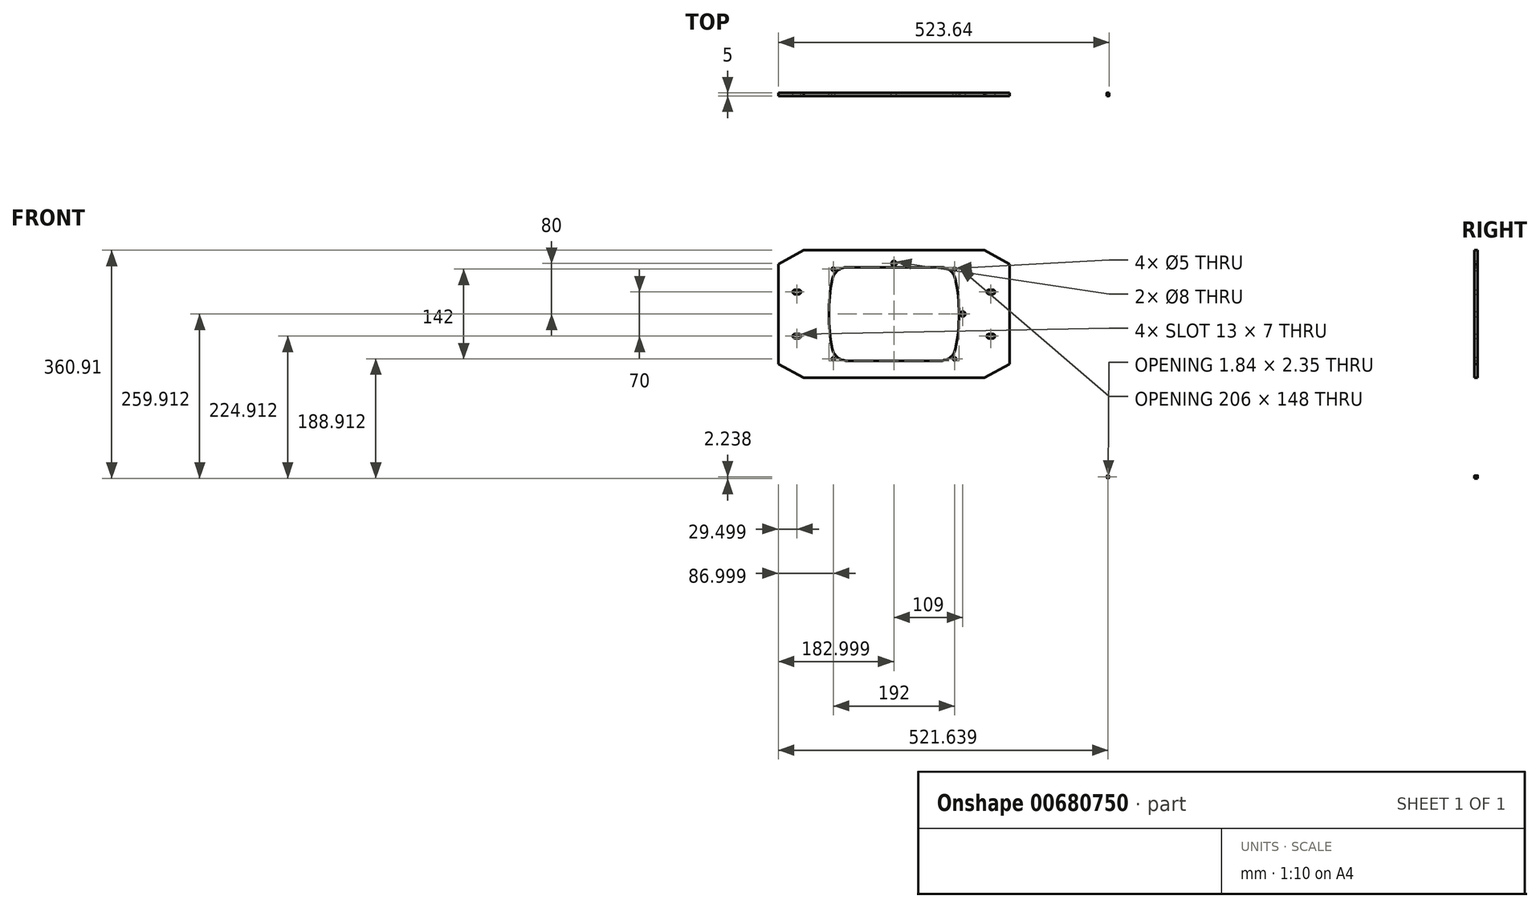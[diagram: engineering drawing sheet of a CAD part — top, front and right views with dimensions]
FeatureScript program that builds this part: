
annotation { "Feature Type Name" : "Feature", "Feature Type Description" : "" }
export const myFeature = defineFeature(function(context is Context, id is Id, definition is map)
    precondition{}
    {
        {
            var Q0;
            Q0=qCreatedBy(makeId("Front.planeOp"),FACE);
            var sketch = newSketch(context, id + "F0", { "sketchPlane" : qUnion([Q0])});
            skFitSpline(sketch, "E0", {"points": [v(706.62, 27.8) * mm, v(706.65, 27.8) * mm, v(706.71, 27.8) * mm, v(706.82, 27.8) * mm, v(707.08, 27.76) * mm, v(707.3, 27.69) * mm, v(707.52, 27.62) * mm, v(707.88, 27.38) * mm, v(708.07, 27.17) * mm, v(708.23, 27) * mm, v(708.36, 26.76) * mm, v(708.5, 26.42) * mm, v(708.6, 26.12) * mm, v(708.63, 25.77) * mm, v(708.65, 25.46) * mm, v(708.6, 25.09) * mm, v(708.56, 24.86) * mm, v(708.36, 24.37) * mm, v(708.23, 24.2) * mm, v(708.05, 23.94) * mm, v(707.84, 23.77) * mm, v(707.61, 23.62) * mm, v(707.37, 23.5) * mm, v(707.09, 23.41) * mm, v(706.82, 23.38) * mm, v(706.47, 23.34) * mm, v(706, 23.49) * mm, v(705.8, 23.57) * mm, v(705.54, 23.73) * mm, v(705.32, 23.92) * mm, v(705.15, 24.07) * mm, v(704.9, 24.49) * mm, v(704.82, 24.73) * mm, v(704.71, 25.11) * mm, v(704.65, 25.38) * mm, v(704.7, 25.99) * mm, v(704.76, 26.27) * mm, v(704.86, 26.62) * mm, v(705, 26.9) * mm, v(705.18, 27.14) * mm, v(705.43, 27.37) * mm, v(705.58, 27.5) * mm, v(706.03, 27.72) * mm, v(706.16, 27.74) * mm, v(706.42, 27.8) * mm, v(706.53, 27.8) * mm, v(706.59, 27.8) * mm, v(706.62, 27.8) * mm]});
            skFitSpline(sketch, "E1", {"points": [v(706.63, 26.75) * mm, v(706.65, 26.75) * mm, v(706.7, 26.75) * mm, v(706.76, 26.75) * mm, v(706.88, 26.73) * mm, v(706.94, 26.7) * mm, v(707.03, 26.67) * mm, v(707.1, 26.64) * mm, v(707.18, 26.57) * mm, v(707.24, 26.52) * mm, v(707.38, 26.35) * mm, v(707.47, 26.15) * mm, v(707.52, 26) * mm, v(707.56, 25.81) * mm, v(707.57, 25.63) * mm, v(707.57, 25.44) * mm, v(707.53, 25.24) * mm, v(707.5, 25.09) * mm, v(707.4, 24.86) * mm, v(707.34, 24.78) * mm, v(707.25, 24.67) * mm, v(707.16, 24.59) * mm, v(707.05, 24.52) * mm, v(706.95, 24.46) * mm, v(706.8, 24.42) * mm, v(706.74, 24.42) * mm, v(706.5, 24.4) * mm, v(706.42, 24.45) * mm, v(706.3, 24.49) * mm, v(706.19, 24.56) * mm, v(706.1, 24.63) * mm, v(706, 24.74) * mm, v(705.95, 24.8) * mm, v(705.85, 25) * mm, v(705.84, 25.03) * mm, v(705.77, 25.24) * mm, v(705.75, 25.44) * mm, v(705.73, 25.49) * mm, v(705.73, 25.73) * mm, v(705.77, 25.95) * mm, v(705.8, 26.05) * mm, v(705.85, 26.18) * mm, v(705.9, 26.29) * mm, v(705.97, 26.4) * mm, v(706.02, 26.47) * mm, v(706.15, 26.6) * mm, v(706.22, 26.64) * mm, v(706.32, 26.7) * mm, v(706.42, 26.72) * mm, v(706.5, 26.75) * mm, v(706.56, 26.75) * mm, v(706.6, 26.75) * mm, v(706.63, 26.75) * mm]});
            skLineSegment(sketch, "E2", {"start": v(225, 182.25) * mm, "end": v(368, 182.25) * mm});
            skLineSegment(sketch, "E3", {"start": v(511, 384.25) * mm, "end": v(389.48, 384.25) * mm});
            skCircle(sketch, "E4", {"center": v(464, 354.25) * mm, "radius": 2.5 * mm});
            skCircle(sketch, "E5", {"center": v(272, 354.25) * mm, "radius": 2.5 * mm});
            skCircle(sketch, "E6", {"center": v(272, 212.25) * mm, "radius": 2.5 * mm});
            skCircle(sketch, "E7", {"center": v(464, 212.25) * mm, "radius": 2.5 * mm});
            skCircle(sketch, "E8", {"center": v(368, 363.25) * mm, "radius": 4 * mm});
            skCircle(sketch, "E9", {"center": v(477, 283.25) * mm, "radius": 4 * mm});
            skLineSegment(sketch, "E10.trimOffspring", {"start": v(368, 182.25) * mm, "end": v(511, 182.25) * mm});
            skLineSegment(sketch, "E11.0", {"start": v(294.06, 357.25) * mm, "end": v(388, 357.25) * mm});
            skLineSegment(sketch, "E11.1", {"start": v(368, 209.25) * mm, "end": v(294.06, 209.25) * mm});
            skArc(sketch, "E11.2", {"start": v(270.55, 228.45) * mm, "mid": v(278.88, 214.66) * mm, "end": v(294.06, 209.25) * mm});
            skArc(sketch, "E11.3", {"start": v(265.34, 296.8) * mm, "mid": v(265.8, 262.46) * mm, "end": v(270.55, 228.45) * mm});
            skArc(sketch, "E11.4", {"start": v(270.55, 338.05) * mm, "mid": v(267.16, 317.52) * mm, "end": v(265.34, 296.8) * mm});
            skLineSegment(sketch, "E11.5", {"start": v(441.96, 209.25) * mm, "end": v(368, 209.25) * mm});
            skArc(sketch, "E11.6", {"start": v(294.06, 357.25) * mm, "mid": v(278.88, 351.84) * mm, "end": v(270.55, 338.05) * mm});
            skArc(sketch, "E11.7", {"start": v(441.96, 209.25) * mm, "mid": v(457.14, 214.66) * mm, "end": v(465.47, 228.45) * mm});
            skArc(sketch, "E11.8", {"start": v(465.47, 228.45) * mm, "mid": v(469.2, 251.8) * mm, "end": v(470.9, 275.36) * mm});
            skArc(sketch, "E11.9", {"start": v(470.9, 275.36) * mm, "mid": v(470, 306.86) * mm, "end": v(465.47, 338.05) * mm});
            skArc(sketch, "E11.10", {"start": v(465.47, 338.05) * mm, "mid": v(457.14, 351.84) * mm, "end": v(441.96, 357.25) * mm});
            skLineSegment(sketch, "E11.11", {"start": v(388, 357.25) * mm, "end": v(441.96, 357.25) * mm});
            skLineSegment(sketch, "E12", {"start": v(368, 363.25) * mm, "end": v(368, 182.25) * mm, "construction": true});
            skLineSegment(sketch, "E13", {"start": v(185, 204.25) * mm, "end": v(185, 362.25) * mm});
            skLineSegment(sketch, "E14", {"start": v(389.48, 384.25) * mm, "end": v(225, 384.25) * mm});
            skLineSegment(sketch, "E15", {"start": v(551, 204.25) * mm, "end": v(551, 362.25) * mm});
            skLineSegment(sketch, "E16", {"start": v(511, 384.25) * mm, "end": v(551, 362.25) * mm});
            skLineSegment(sketch, "E17", {"start": v(551, 362.25) * mm, "end": v(551, 204.25) * mm});
            skLineSegment(sketch, "E18", {"start": v(551, 204.25) * mm, "end": v(511, 182.25) * mm});
            skLineSegment(sketch, "E19", {"start": v(225, 182.25) * mm, "end": v(185, 204.25) * mm});
            skLineSegment(sketch, "E20", {"start": v(185, 362.25) * mm, "end": v(225, 384.25) * mm});
            skPoint(sketch, "E21.orphan", {"position": v(185, 384.25) * mm});
            skPoint(sketch, "E22.orphan", {"position": v(185, 182.25) * mm});
            skPoint(sketch, "E23.orphan", {"position": v(551, 182.25) * mm});
            skLineSegment(sketch, "E24", {"start": v(185, 283.25) * mm, "end": v(551, 283.25) * mm, "construction": true});
            skArc(sketch, "E25", {"start": v(211.5, 321.75) * mm, "mid": v(208, 318.25) * mm, "end": v(211.5, 314.75) * mm});
            skArc(sketch, "E26", {"start": v(217.5, 314.75) * mm, "mid": v(221, 318.25) * mm, "end": v(217.5, 321.75) * mm});
            skLineSegment(sketch, "E27", {"start": v(211.5, 314.75) * mm, "end": v(217.5, 314.75) * mm});
            skLineSegment(sketch, "E28", {"start": v(211.5, 321.75) * mm, "end": v(217.5, 321.75) * mm});
            skArc(sketch, "E29.MirrorCS", {"start": v(217.5, 251.75) * mm, "mid": v(221, 248.25) * mm, "end": v(217.5, 244.75) * mm});
            skLineSegment(sketch, "E30.MirrorCS", {"start": v(211.5, 251.75) * mm, "end": v(217.5, 251.75) * mm});
            skArc(sketch, "E31.MirrorCS", {"start": v(211.5, 244.75) * mm, "mid": v(208, 248.25) * mm, "end": v(211.5, 251.75) * mm});
            skLineSegment(sketch, "E32.MirrorCS", {"start": v(211.5, 244.75) * mm, "end": v(217.5, 244.75) * mm});
            skArc(sketch, "E33.MirrorCS", {"start": v(518.5, 314.75) * mm, "mid": v(515, 318.25) * mm, "end": v(518.5, 321.75) * mm});
            skLineSegment(sketch, "E34.MirrorCS", {"start": v(524.5, 321.75) * mm, "end": v(518.5, 321.75) * mm});
            skArc(sketch, "E35.MirrorCS", {"start": v(524.5, 321.75) * mm, "mid": v(528, 318.25) * mm, "end": v(524.5, 314.75) * mm});
            skLineSegment(sketch, "E36.MirrorCS", {"start": v(524.5, 314.75) * mm, "end": v(518.5, 314.75) * mm});
            skLineSegment(sketch, "E37.MirrorCS", {"start": v(524.5, 251.75) * mm, "end": v(518.5, 251.75) * mm});
            skArc(sketch, "E38.MirrorCS", {"start": v(518.5, 251.75) * mm, "mid": v(515, 248.25) * mm, "end": v(518.5, 244.75) * mm});
            skLineSegment(sketch, "E39.MirrorCS", {"start": v(524.5, 244.75) * mm, "end": v(518.5, 244.75) * mm});
            skArc(sketch, "E40.MirrorCS", {"start": v(524.5, 244.75) * mm, "mid": v(528, 248.25) * mm, "end": v(524.5, 251.75) * mm});
            skSolve(sketch);
        }
        {
            var Q0;
            Q0=qSketchRegion(id+"F0",true);
            extrude(context, id + "F1", {"entities" : qUnion([Q0]), "depth" : 5 * mm, "offsetDistance" : 25.4 * mm});
        }
    });
